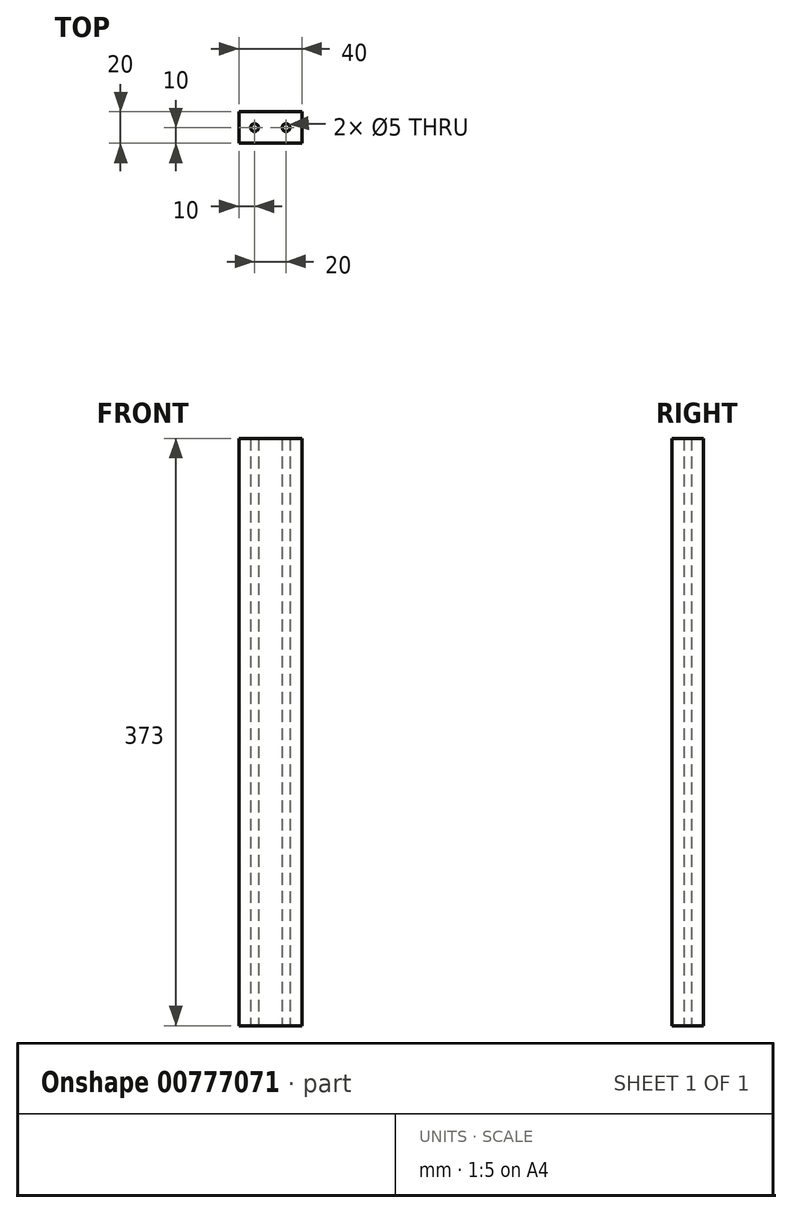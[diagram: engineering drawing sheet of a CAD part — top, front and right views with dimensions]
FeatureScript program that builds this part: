
annotation { "Feature Type Name" : "Feature", "Feature Type Description" : "" }
export const myFeature = defineFeature(function(context is Context, id is Id, definition is map)
    precondition{}
    {
        {
            var Q0;
            Q0=qCreatedBy(makeId("Top.planeOp"),FACE);
            var sketch = newSketch(context, id + "F0", { "sketchPlane" : qUnion([Q0])});
            skLineSegment(sketch, "E0.bottom", {"start": v(-20, 10) * mm, "end": v(20, 10) * mm});
            skLineSegment(sketch, "E0.top", {"start": v(-20, -10) * mm, "end": v(20, -10) * mm});
            skLineSegment(sketch, "E0.left", {"start": v(-20, 10) * mm, "end": v(-20, -10) * mm});
            skLineSegment(sketch, "E0.right", {"start": v(20, 10) * mm, "end": v(20, -10) * mm});
            skCircle(sketch, "E1", {"center": v(-10, 0) * mm, "radius": 2.5 * mm});
            skCircle(sketch, "E2", {"center": v(10, 0) * mm, "radius": 2.5 * mm});
            skSolve(sketch);
        }
        {
            var Q0;
            Q0=qSketchRegion(id+"F0",true);
            extrude(context, id + "F1", {"entities" : qUnion([Q0]), "depth" : (423 - 50) * mm, "offsetDistance" : 25 * mm});
        }
        {
            var Q0;
            Q0=makeQuery(id+"F1.opExtrude","SWEPT_FACE",FACE,{"disambiguationData":[OSD([sQuery(id+"F0.wireOp",EDGE,"E0.right")])]});
            var sketch = newSketch(context, id + "F2", { "sketchPlane" : qUnion([Q0])});
            skCircle(sketch, "E3", {"center": v(0, 10) * mm, "radius": 2.5 * mm});
            skSolve(sketch);
        }
        {
            var Q0;
            Q0=makeQuery(id+"F1.opExtrude","SWEPT_FACE",FACE,{"disambiguationData":[OSD([sQuery(id+"F0.wireOp",EDGE,"E0.top")])]});
            var sketch = newSketch(context, id + "F3", { "sketchPlane" : qUnion([Q0])});
            skCircle(sketch, "E4", {"center": v(0, 186.5) * mm, "radius": 2.5 * mm});
            skPoint(sketch, "E4.centerSnap0", {"position": v(-20, 186.5) * mm});
            skSolve(sketch);
        }
        {
            var Q0;
            Q0=makeQuery(id+"F3.imprint","IMPRINT",FACE,{"disambiguationData":[TD([[makeQuery(id+"F3.imprint","IMPRINT",EDGE,{"derivedFrom":sQuery(id+"F3.wireOp",EDGE,"E4")}),-1.0]])]});
            var sketch = newSketch(context, id + "F4", { "sketchPlane" : qUnion([Q0])});
            skCircle(sketch, "E5", {"center": v(10, 10) * mm, "radius": 2.5 * mm});
            skCircle(sketch, "E6", {"center": v(10, 363) * mm, "radius": 2.5 * mm});
            skSolve(sketch);
        }
    });
